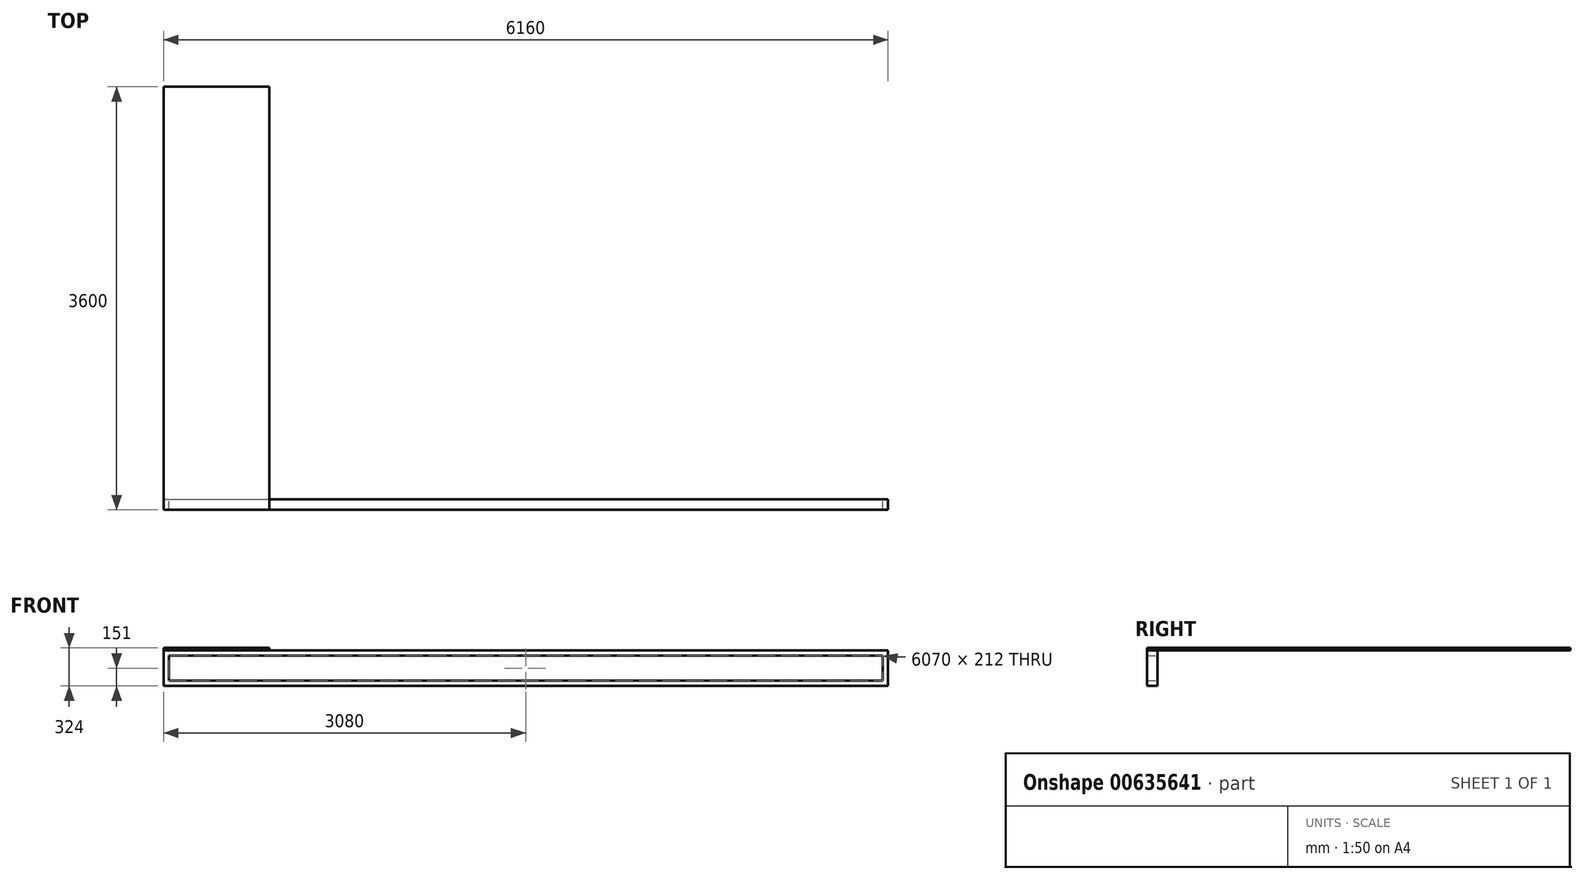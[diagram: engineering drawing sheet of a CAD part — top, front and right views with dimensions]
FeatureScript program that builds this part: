
annotation { "Feature Type Name" : "Feature", "Feature Type Description" : "" }
export const myFeature = defineFeature(function(context is Context, id is Id, definition is map)
    precondition{}
    {
        {
            var Q0;
            Q0=qCreatedBy(makeId("Front.planeOp"),FACE);
            var sketch = newSketch(context, id + "F0", { "sketchPlane" : qUnion([Q0])});
            skLineSegment(sketch, "E0.bottom", {"start": v(0, 0) * mm, "end": v(6160, 0) * mm});
            skLineSegment(sketch, "E0.top", {"start": v(0, 302) * mm, "end": v(6160, 302) * mm});
            skLineSegment(sketch, "E0.left", {"start": v(0, 0) * mm, "end": v(0, 302) * mm});
            skLineSegment(sketch, "E0.right", {"start": v(6160, 0) * mm, "end": v(6160, 302) * mm});
            skLineSegment(sketch, "E1.0", {"start": v(0, 257) * mm, "end": v(6160, 257) * mm});
            skLineSegment(sketch, "E2.0", {"start": v(0, 45) * mm, "end": v(6160, 45) * mm});
            skLineSegment(sketch, "E3.0", {"start": v(45, 45) * mm, "end": v(45, 257) * mm});
            skLineSegment(sketch, "E4.0", {"start": v(6115, 45) * mm, "end": v(6115, 257) * mm});
            skLineSegment(sketch, "E5.bottom", {"start": v(3057.5, 45) * mm, "end": v(3102.5, 45) * mm});
            skLineSegment(sketch, "E5.top", {"start": v(3057.5, 257) * mm, "end": v(3102.5, 257) * mm});
            skLineSegment(sketch, "E5.left", {"start": v(3057.5, 45) * mm, "end": v(3057.5, 257) * mm});
            skLineSegment(sketch, "E5.right", {"start": v(3102.5, 45) * mm, "end": v(3102.5, 257) * mm});
            skLineSegment(sketch, "E6", {"start": v(3080, 45) * mm, "end": v(3080, 257) * mm, "construction": true});
            skLineSegment(sketch, "E7", {"start": v(3080, 302) * mm, "end": v(3080, 0) * mm, "construction": true});
            skSolve(sketch);
        }
        {
            var Q0;
            {var subQ6=sQuery(id+"F0.wireOp",EDGE,"E0.top");Q0=makeQuery(id+"F0.imprint","IMPRINT",FACE,{"disambiguationData":[TD([[makeQuery(id+"F0.imprint","IMPRINT",EDGE,{"derivedFrom":subQ6}),-1.0]])]});}
            var Q1;
            {var subQ4=sQuery(id+"F0.wireOp",EDGE,"E0.bottom");Q1=makeQuery(id+"F0.imprint","IMPRINT",FACE,{"disambiguationData":[TD([[makeQuery(id+"F0.imprint","IMPRINT",EDGE,{"derivedFrom":subQ4}),1.0]])]});}
            var Q2;
            {var subQ5=sQuery(id+"F0.wireOp",EDGE,"E3.0");Q2=makeQuery(id+"F0.imprint","IMPRINT",FACE,{"disambiguationData":[TD([[makeQuery(id+"F0.imprint","IMPRINT",EDGE,{"derivedFrom":subQ5}),1.0]])]});}
            var Q3;
            Q3=makeQuery(id+"F0.imprint","IMPRINT",FACE,{"disambiguationData":[TD([[makeQuery(id+"F0.imprint","IMPRINT",EDGE,{"derivedFrom":sQuery(id+"F0.wireOp",EDGE,"E5.bottom")}),1.0]])]});
            var Q4;
            {var subQ5=sQuery(id+"F0.wireOp",EDGE,"E4.0");Q4=makeQuery(id+"F0.imprint","IMPRINT",FACE,{"disambiguationData":[TD([[makeQuery(id+"F0.imprint","IMPRINT",EDGE,{"derivedFrom":subQ5}),-1.0]])]});}
            extrude(context, id + "F1", {"entities" : qUnion([Q0, Q1, Q2, Q3, Q4]), "depth" : 90 * mm, "offsetDistance" : 25 * mm});
        }
        {
            var Q0;
            Q0=makeQuery(id+"F1.opExtrude","SWEPT_FACE",FACE,{"disambiguationData":[OSD([sQuery(id+"F0.wireOp",EDGE,"E0.top")])]});
            var sketch = newSketch(context, id + "F2", { "sketchPlane" : qUnion([Q0])});
            skLineSegment(sketch, "E8.bottom", {"start": v(0, -90) * mm, "end": v(900, -90) * mm});
            skLineSegment(sketch, "E8.top", {"start": v(0, 3510) * mm, "end": v(900, 3510) * mm});
            skLineSegment(sketch, "E8.left", {"start": v(0, -90) * mm, "end": v(0, 3510) * mm});
            skLineSegment(sketch, "E8.right", {"start": v(900, -90) * mm, "end": v(900, 3510) * mm});
            skSolve(sketch);
        }
        {
            var Q0;
            Q0 = qSketchRegion(id + "F2", true);
            extrude(context, id + "F3", {"entities" : qUnion([Q0]), "depth" : 22 * mm, "offsetDistance" : 25 * mm});
        }
    });
